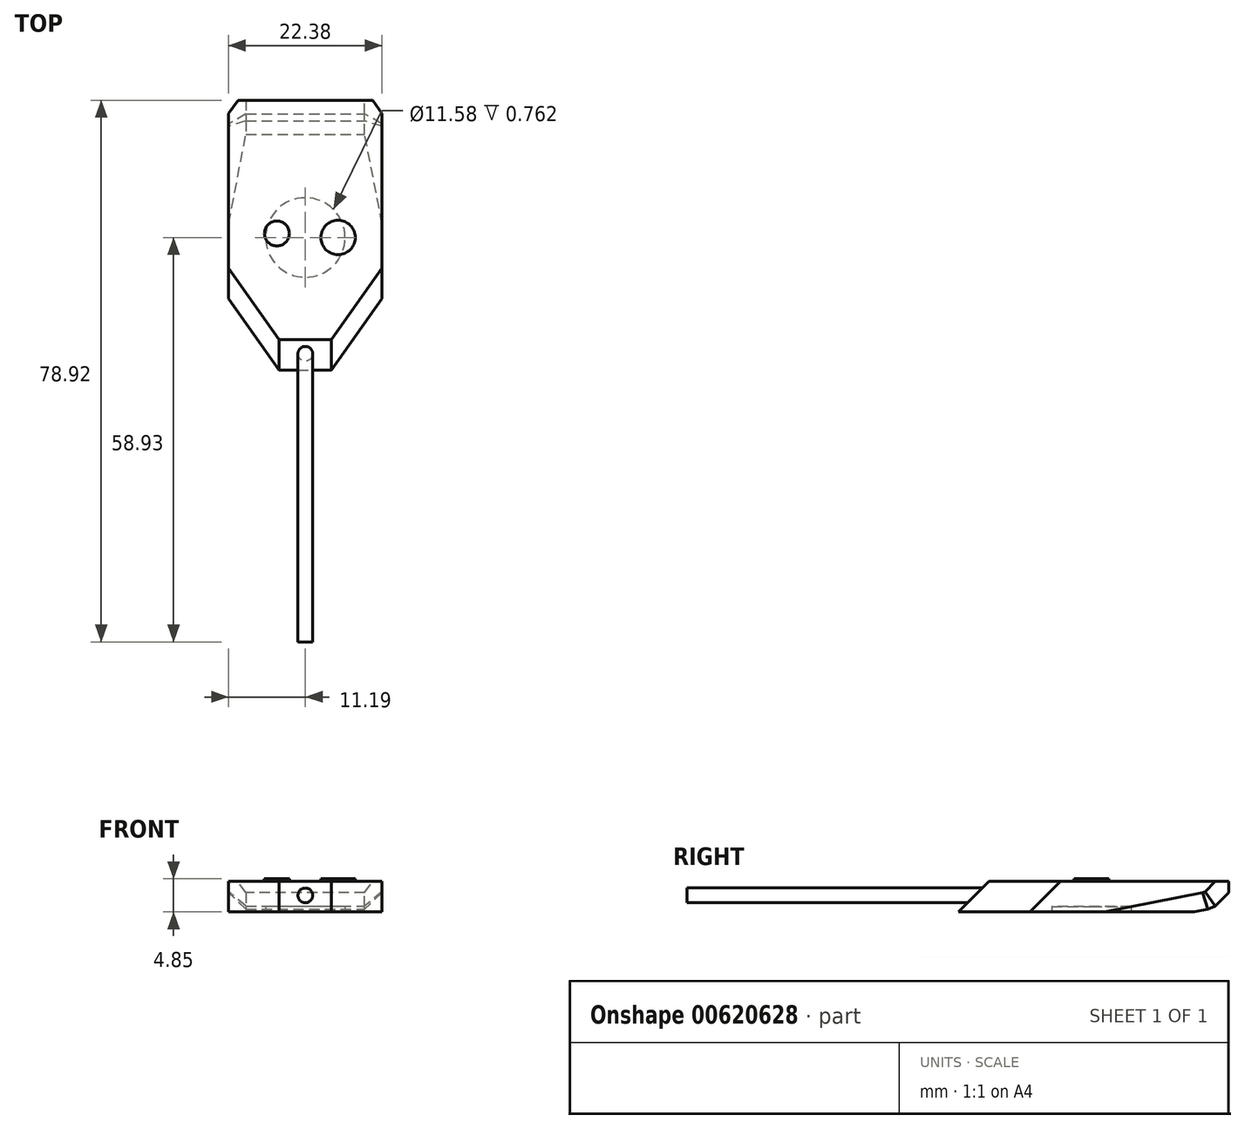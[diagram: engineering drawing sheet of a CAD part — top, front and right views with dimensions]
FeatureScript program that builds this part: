
annotation { "Feature Type Name" : "Feature", "Feature Type Description" : "" }
export const myFeature = defineFeature(function(context is Context, id is Id, definition is map)
    precondition{}
    {
        {
            var Q0;
            Q0=qCreatedBy(makeId("Top.planeOp"),FACE);
            var sketch = newSketch(context, id + "F0", { "sketchPlane" : qUnion([Q0])});
            skLineSegment(sketch, "E0.bottom", {"start": v(11.19, -19.99) * mm, "end": v(-11.19, -19.99) * mm});
            skLineSegment(sketch, "E0.top", {"start": v(11.19, 19.99) * mm, "end": v(-11.19, 19.99) * mm});
            skLineSegment(sketch, "E0.left", {"start": v(11.19, -19.99) * mm, "end": v(11.19, 19.99) * mm});
            skLineSegment(sketch, "E0.right", {"start": v(-11.19, -19.99) * mm, "end": v(-11.19, 19.99) * mm});
            skPoint(sketch, "E0.middle", {"position": v(0, 0) * mm});
            skSolve(sketch);
        }
        {
            var Q0;
            Q0=makeQuery(id+"F0.imprint","IMPRINT",FACE,{"disambiguationData":[TD([[makeQuery(id+"F0.imprint","IMPRINT",EDGE,{"derivedFrom":sQuery(id+"F0.wireOp",EDGE,"E0.bottom")}),-1.0]])]});
            extrude(context, id + "F1", {"entities" : qUnion([Q0]), "depth" : 4.44 * mm, "offsetDistance" : 25.4 * mm});
        }
        {
            var Q0;
            Q0=makeQuery(id+"F1.opExtrude","CAP_EDGE",EDGE,{"disambiguationData":[OSD([sQuery(id+"F0.wireOp",EDGE,"E0.bottom")])],"isStart":false});
            chamfer(context, id + "F2", {"entities" : qUnion([Q0]), "width" : 5.08 * mm, "tangentPropagation" : true});
        }
        {
            var Q0;
            Q0=makeQuery(id+"F2.opChamfer","BLEND_EDGE",EDGE,{"blendedFrom":[makeQuery(id+"F1.opExtrude","CAP_EDGE",EDGE,{"disambiguationData":[OSD([sQuery(id+"F0.wireOp",EDGE,"E0.bottom")])],"isStart":false}),makeQuery(id+"F1.opExtrude","SWEPT_FACE",FACE,{"disambiguationData":[OSD([sQuery(id+"F0.wireOp",EDGE,"E0.left")])]})],"blendedInto":[makeQuery(id+"F1.opExtrude","SWEPT_FACE",FACE,{"disambiguationData":[OSD([sQuery(id+"F0.wireOp",EDGE,"E0.left")])]})]});
            var Q1;
            Q1=makeQuery(id+"F2.opChamfer","BLEND_EDGE",EDGE,{"blendedFrom":[makeQuery(id+"F1.opExtrude","CAP_EDGE",EDGE,{"disambiguationData":[OSD([sQuery(id+"F0.wireOp",EDGE,"E0.bottom")])],"isStart":false}),makeQuery(id+"F1.opExtrude","SWEPT_FACE",FACE,{"disambiguationData":[OSD([sQuery(id+"F0.wireOp",EDGE,"E0.right")])]})],"blendedInto":[makeQuery(id+"F1.opExtrude","SWEPT_FACE",FACE,{"disambiguationData":[OSD([sQuery(id+"F0.wireOp",EDGE,"E0.right")])]})]});
            chamfer(context, id + "F3", {"entities" : qUnion([Q0, Q1]), "width" : 7.37 * mm, "tangentPropagation" : true});
        }
        {
            var Q0;
            Q0=makeQuery(id+"F1.opExtrude","CAP_EDGE",EDGE,{"disambiguationData":[OSD([sQuery(id+"F0.wireOp",EDGE,"E0.top")])],"isStart":true});
            chamfer(context, id + "F4", {"entities" : qUnion([Q0]), "width" : 2.8 * mm, "tangentPropagation" : true});
        }
        {
            var Q0;
            {var subQ0=sQuery(id+"F0.wireOp",EDGE,"E0.top");Q0=makeQuery(id+"F4.opChamfer","BLEND_EDGE",EDGE,{"blendedFrom":[makeQuery(id+"F1.opExtrude","CAP_EDGE",EDGE,{"disambiguationData":[OSD([subQ0])],"isStart":true}),makeQuery(id+"F1.opExtrude","CAP_FACE",FACE,{"disambiguationData":[OSD([sQuery(id+"F0.wireOp",EDGE,"E0.bottom"),subQ0,sQuery(id+"F0.wireOp",EDGE,"E0.left"),sQuery(id+"F0.wireOp",EDGE,"E0.right")])],"isStart":true})],"blendedInto":[makeQuery(id+"F1.opExtrude","CAP_FACE",FACE,{"disambiguationData":[OSD([sQuery(id+"F0.wireOp",EDGE,"E0.bottom"),subQ0,sQuery(id+"F0.wireOp",EDGE,"E0.left"),sQuery(id+"F0.wireOp",EDGE,"E0.right")])],"isStart":true})]});}
            chamfer(context, id + "F5", {"entities" : qUnion([Q0]), "width" : 2.8 * mm, "tangentPropagation" : true});
        }
        {
            var Q0;
            Q0=qCreatedBy(makeId("Top.planeOp"),FACE);
            var sketch = newSketch(context, id + "F6", { "sketchPlane" : qUnion([Q0])});
            skCircle(sketch, "E1", {"center": v(0, 0) * mm, "radius": 5.8 * mm});
            skSolve(sketch);
        }
        {
            var Q0;
            Q0=makeQuery(id+"F6.imprint","IMPRINT",FACE,{"disambiguationData":[TD([[makeQuery(id+"F6.imprint","IMPRINT",EDGE,{"derivedFrom":sQuery(id+"F6.wireOp",EDGE,"E1")}),1.0]])]});
            var Q1;
            Q1=sQuery(id+"F6.wireOp",EDGE,"E1");
            extrude(context, id + "F7", {"entities" : qUnion([Q0]), "operationType" : NewBodyOperationType.REMOVE, "surfaceEntities" : qUnion([Q1]), "depth" : 0.76 * mm, "offsetDistance" : 25.4 * mm});
        }
        {
            var Q0;
            Q0=qCreatedBy(makeId("Front.planeOp"),FACE);
            var sketch = newSketch(context, id + "F8", { "sketchPlane" : qUnion([Q0])});
            skCircle(sketch, "E2", {"center": v(0, 2.4) * mm, "radius": 1.08 * mm});
            skSolve(sketch);
        }
        {
            var Q0;
            Q0 = qSketchRegion(id + "F8", true);
            extrude(context, id + "F9", {"entities" : qUnion([Q0]), "operationType" : NewBodyOperationType.ADD, "depth" : 58.93 * mm, "offsetDistance" : 25.4 * mm});
        }
        {
            var Q0;
            Q0=makeQuery(id+"F1.opExtrude","CAP_FACE",FACE,{"disambiguationData":[OSD([sQuery(id+"F0.wireOp",EDGE,"E0.bottom"),sQuery(id+"F0.wireOp",EDGE,"E0.top"),sQuery(id+"F0.wireOp",EDGE,"E0.left"),sQuery(id+"F0.wireOp",EDGE,"E0.right")])],"isStart":false});
            var sketch = newSketch(context, id + "F10", { "sketchPlane" : qUnion([Q0])});
            skCircle(sketch, "E3", {"center": v(4.77, 0) * mm, "radius": 2.51 * mm});
            skCircle(sketch, "E4", {"center": v(-4.15, 0.58) * mm, "radius": 1.81 * mm});
            skSolve(sketch);
        }
        {
            var Q0;
            Q0=makeQuery(id+"F10.imprint","IMPRINT",FACE,{"disambiguationData":[TD([[makeQuery(id+"F10.imprint","IMPRINT",EDGE,{"derivedFrom":sQuery(id+"F10.wireOp",EDGE,"E4")}),1.0]])]});
            var Q1;
            Q1=makeQuery(id+"F10.imprint","IMPRINT",FACE,{"disambiguationData":[TD([[makeQuery(id+"F10.imprint","IMPRINT",EDGE,{"derivedFrom":sQuery(id+"F10.wireOp",EDGE,"E3")}),1.0]])]});
            extrude(context, id + "F11", {"entities" : qUnion([Q0, Q1]), "operationType" : NewBodyOperationType.ADD, "depth" : 0.4 * mm, "offsetDistance" : 25.4 * mm});
        }
        {
            var Q0;
            {var subQ0=sQuery(id+"F0.wireOp",EDGE,"E0.top");var subQ1=makeQuery(id+"F1.opExtrude","CAP_FACE",FACE,{"disambiguationData":[OSD([sQuery(id+"F0.wireOp",EDGE,"E0.bottom"),subQ0,sQuery(id+"F0.wireOp",EDGE,"E0.left"),sQuery(id+"F0.wireOp",EDGE,"E0.right")])],"isStart":true});Q0=makeQuery(id+"F5.opChamfer","BLEND_EDGE",EDGE,{"blendedFrom":[makeQuery(id+"F4.opChamfer","BLEND_EDGE",EDGE,{"blendedFrom":[makeQuery(id+"F1.opExtrude","CAP_EDGE",EDGE,{"disambiguationData":[OSD([subQ0])],"isStart":true}),subQ1],"blendedInto":[subQ1]}),subQ1],"blendedInto":[subQ1]});}
            chamfer(context, id + "F12", {"entities" : qUnion([Q0]), "width" : 5.08 * mm, "tangentPropagation" : true});
        }
        {
            var Q0;
            {var subQ0=sQuery(id+"F0.wireOp",EDGE,"E0.left");var subQ1=sQuery(id+"F0.wireOp",EDGE,"E0.top");var subQ2=makeQuery(id+"F1.opExtrude","CAP_FACE",FACE,{"disambiguationData":[OSD([sQuery(id+"F0.wireOp",EDGE,"E0.bottom"),subQ1,subQ0,sQuery(id+"F0.wireOp",EDGE,"E0.right")])],"isStart":true});Q0=makeQuery(id+"F12.opChamfer","BLEND_EDGE",EDGE,{"blendedFrom":[makeQuery(id+"F5.opChamfer","BLEND_EDGE",EDGE,{"blendedFrom":[makeQuery(id+"F4.opChamfer","BLEND_EDGE",EDGE,{"blendedFrom":[makeQuery(id+"F1.opExtrude","CAP_EDGE",EDGE,{"disambiguationData":[OSD([subQ1])],"isStart":true}),subQ2],"blendedInto":[subQ2]}),subQ2],"blendedInto":[subQ2]}),makeQuery(id+"F1.opExtrude","SWEPT_FACE",FACE,{"disambiguationData":[OSD([subQ0])]})],"blendedInto":[makeQuery(id+"F1.opExtrude","SWEPT_FACE",FACE,{"disambiguationData":[OSD([subQ0])]})]});}
            var Q1;
            {var subQ0=sQuery(id+"F0.wireOp",EDGE,"E0.right");var subQ1=sQuery(id+"F0.wireOp",EDGE,"E0.top");var subQ2=makeQuery(id+"F1.opExtrude","CAP_FACE",FACE,{"disambiguationData":[OSD([sQuery(id+"F0.wireOp",EDGE,"E0.bottom"),subQ1,sQuery(id+"F0.wireOp",EDGE,"E0.left"),subQ0])],"isStart":true});Q1=makeQuery(id+"F12.opChamfer","BLEND_EDGE",EDGE,{"blendedFrom":[makeQuery(id+"F5.opChamfer","BLEND_EDGE",EDGE,{"blendedFrom":[makeQuery(id+"F4.opChamfer","BLEND_EDGE",EDGE,{"blendedFrom":[makeQuery(id+"F1.opExtrude","CAP_EDGE",EDGE,{"disambiguationData":[OSD([subQ1])],"isStart":true}),subQ2],"blendedInto":[subQ2]}),subQ2],"blendedInto":[subQ2]}),makeQuery(id+"F1.opExtrude","SWEPT_FACE",FACE,{"disambiguationData":[OSD([subQ0])]})],"blendedInto":[makeQuery(id+"F1.opExtrude","SWEPT_FACE",FACE,{"disambiguationData":[OSD([subQ0])]})]});}
            var Q2;
            Q2=makeQuery(id+"F4.opChamfer","BLEND_EDGE",EDGE,{"blendedFrom":[makeQuery(id+"F1.opExtrude","CAP_EDGE",EDGE,{"disambiguationData":[OSD([sQuery(id+"F0.wireOp",EDGE,"E0.top")])],"isStart":true}),makeQuery(id+"F1.opExtrude","SWEPT_FACE",FACE,{"disambiguationData":[OSD([sQuery(id+"F0.wireOp",EDGE,"E0.right")])]})],"blendedInto":[makeQuery(id+"F1.opExtrude","SWEPT_FACE",FACE,{"disambiguationData":[OSD([sQuery(id+"F0.wireOp",EDGE,"E0.right")])]})]});
            var Q3;
            {var subQ0=sQuery(id+"F0.wireOp",EDGE,"E0.right");var subQ1=sQuery(id+"F0.wireOp",EDGE,"E0.top");Q3=makeQuery(id+"F5.opChamfer","BLEND_EDGE",EDGE,{"blendedFrom":[makeQuery(id+"F4.opChamfer","BLEND_EDGE",EDGE,{"blendedFrom":[makeQuery(id+"F1.opExtrude","CAP_EDGE",EDGE,{"disambiguationData":[OSD([subQ1])],"isStart":true}),makeQuery(id+"F1.opExtrude","CAP_FACE",FACE,{"disambiguationData":[OSD([sQuery(id+"F0.wireOp",EDGE,"E0.bottom"),subQ1,sQuery(id+"F0.wireOp",EDGE,"E0.left"),subQ0])],"isStart":true})],"blendedInto":[makeQuery(id+"F1.opExtrude","CAP_FACE",FACE,{"disambiguationData":[OSD([sQuery(id+"F0.wireOp",EDGE,"E0.bottom"),subQ1,sQuery(id+"F0.wireOp",EDGE,"E0.left"),subQ0])],"isStart":true})]}),makeQuery(id+"F1.opExtrude","SWEPT_FACE",FACE,{"disambiguationData":[OSD([subQ0])]})],"blendedInto":[makeQuery(id+"F1.opExtrude","SWEPT_FACE",FACE,{"disambiguationData":[OSD([subQ0])]})]});}
            var Q4;
            {var subQ0=sQuery(id+"F0.wireOp",EDGE,"E0.left");var subQ1=sQuery(id+"F0.wireOp",EDGE,"E0.top");Q4=makeQuery(id+"F5.opChamfer","BLEND_EDGE",EDGE,{"blendedFrom":[makeQuery(id+"F4.opChamfer","BLEND_EDGE",EDGE,{"blendedFrom":[makeQuery(id+"F1.opExtrude","CAP_EDGE",EDGE,{"disambiguationData":[OSD([subQ1])],"isStart":true}),makeQuery(id+"F1.opExtrude","CAP_FACE",FACE,{"disambiguationData":[OSD([sQuery(id+"F0.wireOp",EDGE,"E0.bottom"),subQ1,subQ0,sQuery(id+"F0.wireOp",EDGE,"E0.right")])],"isStart":true})],"blendedInto":[makeQuery(id+"F1.opExtrude","CAP_FACE",FACE,{"disambiguationData":[OSD([sQuery(id+"F0.wireOp",EDGE,"E0.bottom"),subQ1,subQ0,sQuery(id+"F0.wireOp",EDGE,"E0.right")])],"isStart":true})]}),makeQuery(id+"F1.opExtrude","SWEPT_FACE",FACE,{"disambiguationData":[OSD([subQ0])]})],"blendedInto":[makeQuery(id+"F1.opExtrude","SWEPT_FACE",FACE,{"disambiguationData":[OSD([subQ0])]})]});}
            var Q5;
            Q5=makeQuery(id+"F4.opChamfer","BLEND_EDGE",EDGE,{"blendedFrom":[makeQuery(id+"F1.opExtrude","CAP_EDGE",EDGE,{"disambiguationData":[OSD([sQuery(id+"F0.wireOp",EDGE,"E0.top")])],"isStart":true}),makeQuery(id+"F1.opExtrude","SWEPT_FACE",FACE,{"disambiguationData":[OSD([sQuery(id+"F0.wireOp",EDGE,"E0.left")])]})],"blendedInto":[makeQuery(id+"F1.opExtrude","SWEPT_FACE",FACE,{"disambiguationData":[OSD([sQuery(id+"F0.wireOp",EDGE,"E0.left")])]})]});
            chamfer(context, id + "F13", {"entities" : qUnion([Q0, Q1, Q2, Q3, Q4, Q5]), "width" : 2.54 * mm, "tangentPropagation" : true});
        }
    });
